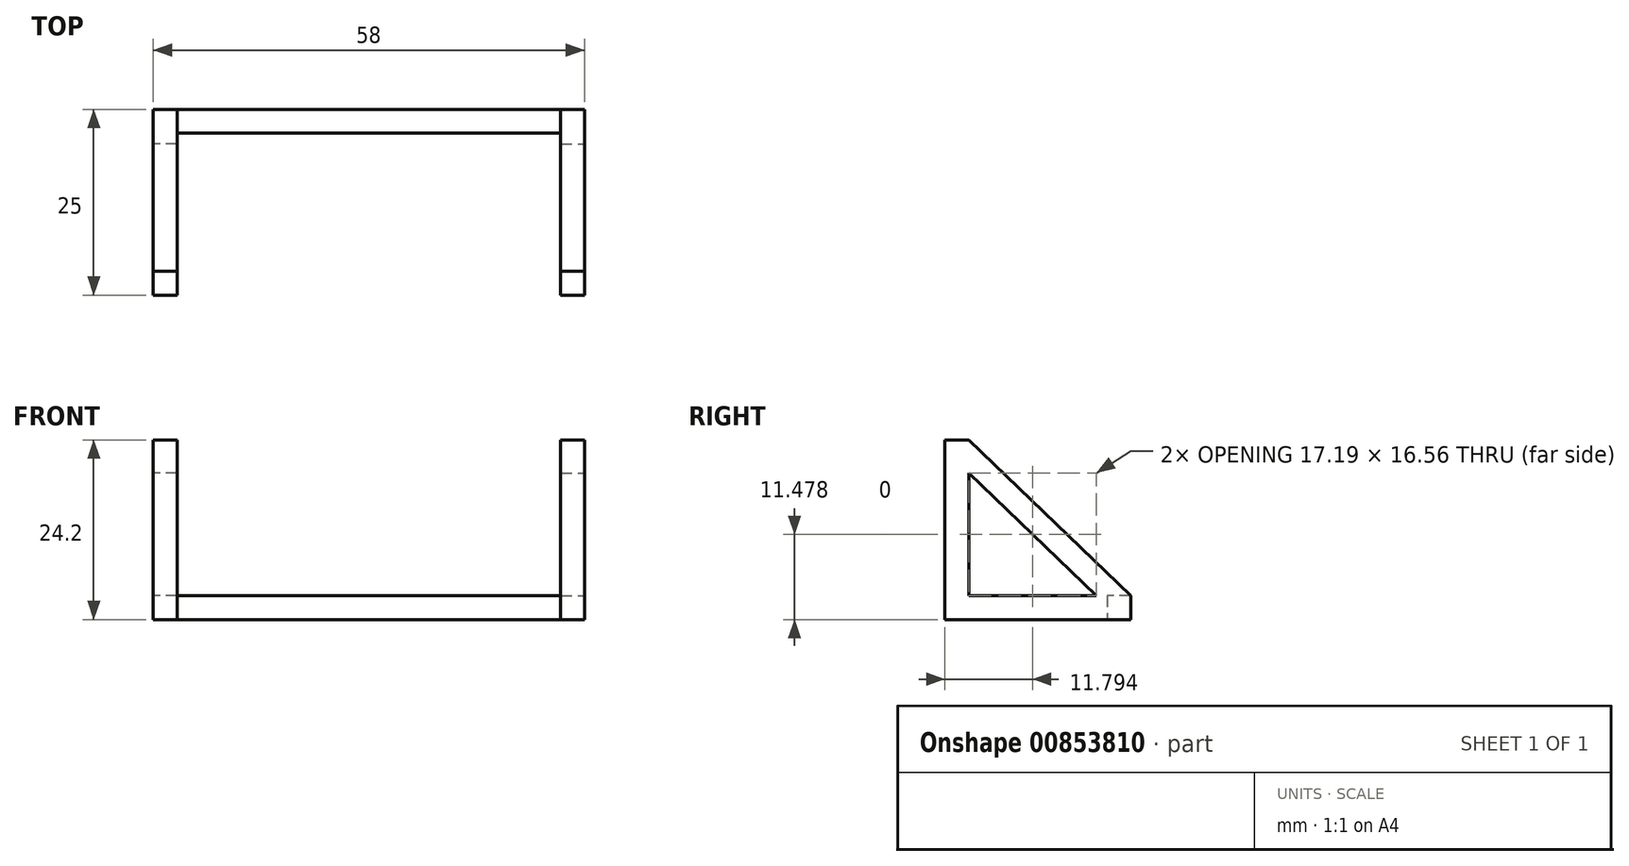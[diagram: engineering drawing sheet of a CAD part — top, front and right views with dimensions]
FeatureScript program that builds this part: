
annotation { "Feature Type Name" : "Feature", "Feature Type Description" : "" }
export const myFeature = defineFeature(function(context is Context, id is Id, definition is map)
    precondition{}
    {
        {
            var Q0;
            Q0=qCreatedBy(makeId("Top.planeOp"),FACE);
            var sketch = newSketch(context, id + "F0", { "sketchPlane" : qUnion([Q0])});
            skLineSegment(sketch, "E0.bottom", {"start": v(-28.2, 25) * mm, "end": v(29.8, 25) * mm});
            skLineSegment(sketch, "E0.left", {"start": v(-28.2, 25) * mm, "end": v(-28.2, 0) * mm});
            skLineSegment(sketch, "E0.right", {"start": v(29.8, 25) * mm, "end": v(29.8, 0) * mm});
            skLineSegment(sketch, "E1.bottom", {"start": v(-25, 21.8) * mm, "end": v(26.6, 21.8) * mm});
            skLineSegment(sketch, "E1.left", {"start": v(-25, 21.8) * mm, "end": v(-25, 0) * mm});
            skLineSegment(sketch, "E1.right", {"start": v(26.6, 21.8) * mm, "end": v(26.6, 0) * mm});
            skLineSegment(sketch, "E2", {"start": v(-28.2, 0) * mm, "end": v(-25, 0) * mm});
            skLineSegment(sketch, "E3", {"start": v(26.6, 0) * mm, "end": v(29.8, 0) * mm});
            skSolve(sketch);
        }
        {
            var Q0;
            Q0=makeQuery(id+"F0.imprint","IMPRINT",FACE,{"disambiguationData":[TD([[makeQuery(id+"F0.imprint","IMPRINT",EDGE,{"derivedFrom":sQuery(id+"F0.wireOp",EDGE,"E0.bottom")}),-1.0]])]});
            extrude(context, id + "F1", {"entities" : qUnion([Q0]), "depth" : 3.2 * mm, "offsetDistance" : 25 * mm});
        }
        {
            var Q0;
            Q0=makeQuery(id+"F1.opExtrude","SWEPT_FACE",FACE,{"disambiguationData":[OSD([sQuery(id+"F0.wireOp",EDGE,"E0.right")])]});
            var sketch = newSketch(context, id + "F2", { "sketchPlane" : qUnion([Q0])});
            skLineSegment(sketch, "E4.bottom", {"start": v(0, 3.2) * mm, "end": v(3.2, 3.2) * mm});
            skLineSegment(sketch, "E4.top", {"start": v(0, 24.2) * mm, "end": v(3.2, 24.2) * mm});
            skLineSegment(sketch, "E4.left", {"start": v(0, 3.2) * mm, "end": v(0, 24.2) * mm});
            skLineSegment(sketch, "E4.right", {"start": v(3.2, 3.2) * mm, "end": v(3.2, 24.2) * mm});
            skLineSegment(sketch, "E5", {"start": v(3.2, 24.2) * mm, "end": v(25, 3.2) * mm});
            skLineSegment(sketch, "E6", {"start": v(20.39, 3.2) * mm, "end": v(3.2, 19.76) * mm});
            skSolve(sketch);
        }
        {
            var Q0;
            {var subQ1=sQuery(id+"F2.wireOp",EDGE,"E4.bottom");Q0=makeQuery(id+"F2.imprint","IMPRINT",FACE,{"disambiguationData":[TD([[makeQuery(id+"F2.imprint","IMPRINT",EDGE,{"derivedFrom":subQ1}),-1.0]])]});}
            var Q1;
            {var subQ0=sQuery(id+"F2.wireOp",EDGE,"E5");Q1=makeQuery(id+"F2.imprint","IMPRINT",FACE,{"disambiguationData":[TD([[makeQuery(id+"F2.imprint","IMPRINT",EDGE,{"derivedFrom":subQ0}),-1.0]])]});}
            extrude(context, id + "F3", {"entities" : qUnion([Q0, Q1]), "operationType" : NewBodyOperationType.ADD, "oppositeDirection" : true, "depth" : 3.2 * mm, "offsetDistance" : 25 * mm});
        }
        {
            var Q0;
            Q0=makeQuery(id+"F1.opExtrude","SWEPT_FACE",FACE,{"disambiguationData":[OSD([sQuery(id+"F0.wireOp",EDGE,"E0.left")])]});
            var sketch = newSketch(context, id + "F4", { "sketchPlane" : qUnion([Q0])});
            skLineSegment(sketch, "E7.bottom", {"start": v(0, 3.2) * mm, "end": v(-3.2, 3.2) * mm});
            skLineSegment(sketch, "E7.top", {"start": v(0, 24.2) * mm, "end": v(-3.2, 24.2) * mm});
            skLineSegment(sketch, "E7.left", {"start": v(0, 3.2) * mm, "end": v(0, 24.2) * mm});
            skLineSegment(sketch, "E7.right", {"start": v(-3.2, 3.2) * mm, "end": v(-3.2, 24.2) * mm});
            skLineSegment(sketch, "E8", {"start": v(-3.2, 24.2) * mm, "end": v(-25, 3.2) * mm});
            skLineSegment(sketch, "E9", {"start": v(-20.39, 3.2) * mm, "end": v(-3.2, 19.76) * mm});
            skSolve(sketch);
        }
        {
            var Q0;
            {var subQ0=sQuery(id+"F4.wireOp",EDGE,"E8");Q0=makeQuery(id+"F4.imprint","IMPRINT",FACE,{"disambiguationData":[TD([[makeQuery(id+"F4.imprint","IMPRINT",EDGE,{"derivedFrom":subQ0}),1.0]])]});}
            var Q1;
            {var subQ1=sQuery(id+"F4.wireOp",EDGE,"E7.bottom");Q1=makeQuery(id+"F4.imprint","IMPRINT",FACE,{"disambiguationData":[TD([[makeQuery(id+"F4.imprint","IMPRINT",EDGE,{"derivedFrom":subQ1}),1.0]])]});}
            extrude(context, id + "F5", {"entities" : qUnion([Q0, Q1]), "operationType" : NewBodyOperationType.ADD, "oppositeDirection" : true, "depth" : 3.2 * mm, "offsetDistance" : 25 * mm});
        }
    });
